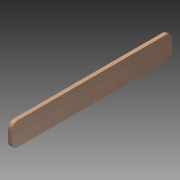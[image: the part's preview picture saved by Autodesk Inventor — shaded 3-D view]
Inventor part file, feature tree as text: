
AUTODESK INVENTOR PART (.ipt)
format: ipt  version: 2013 (Build 170138000, 138)  size: 89,600 bytes
history: native  units: in
note: dims shown in document units (in); Inventor stores cm internally (conversion verified against a paired STEP export)
features: extrude x1, fillet x1, sketch x1
ambient origin geometry x8: Origin, YZ Plane, XZ Plane, XY Plane, X Axis, Y Axis, Z Axis, Center Point
bodies: Solid1 (feature_tree)
feature tree (3):
  extrude  "Extrusion1"  Depth=0.75in
  fillet  "Fillet1"  Radius=34.5in
  sketch  "Sketch1"  dims[d0=5.0in d1=0.75in d2=34.5in d3=0.0in d4=1.3125in]
